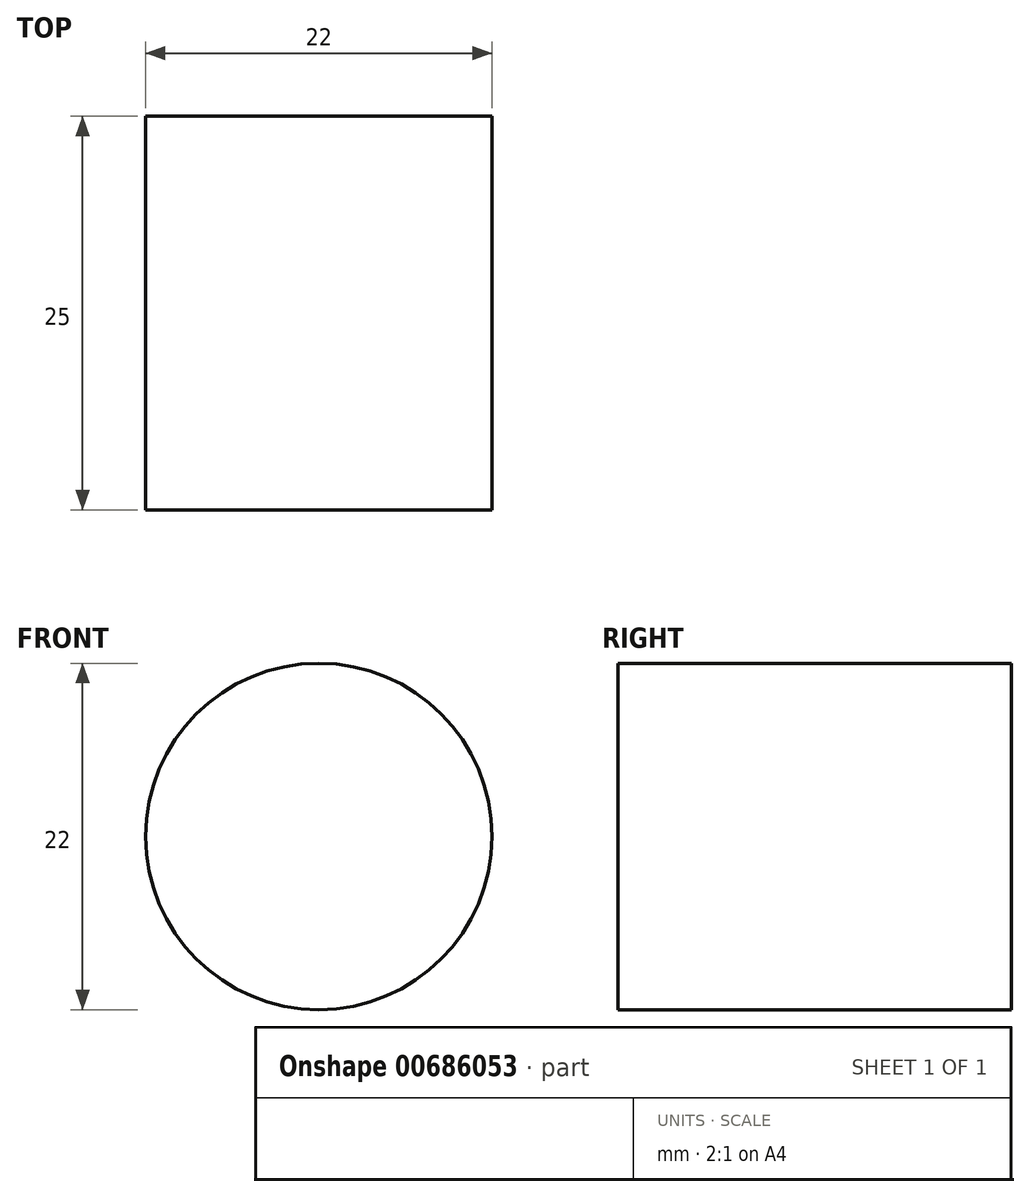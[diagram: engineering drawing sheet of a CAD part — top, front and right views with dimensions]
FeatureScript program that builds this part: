
annotation { "Feature Type Name" : "Feature", "Feature Type Description" : "" }
export const myFeature = defineFeature(function(context is Context, id is Id, definition is map)
    precondition{}
    {
        {
            var Q0;
            Q0=qCreatedBy(makeId("Front.planeOp"),FACE);
            var sketch = newSketch(context, id + "F0", { "sketchPlane" : qUnion([Q0])});
            skCircle(sketch, "E0", {"center": v(0, 0) * mm, "radius": 11 * mm});
            skSolve(sketch);
        }
        {
            var Q0;
            Q0 = qSketchRegion(id + "F0", true);
            extrude(context, id + "F1", {"entities" : qUnion([Q0]), "depth" : 25 * mm, "offsetDistance" : 25 * mm});
        }
    });
